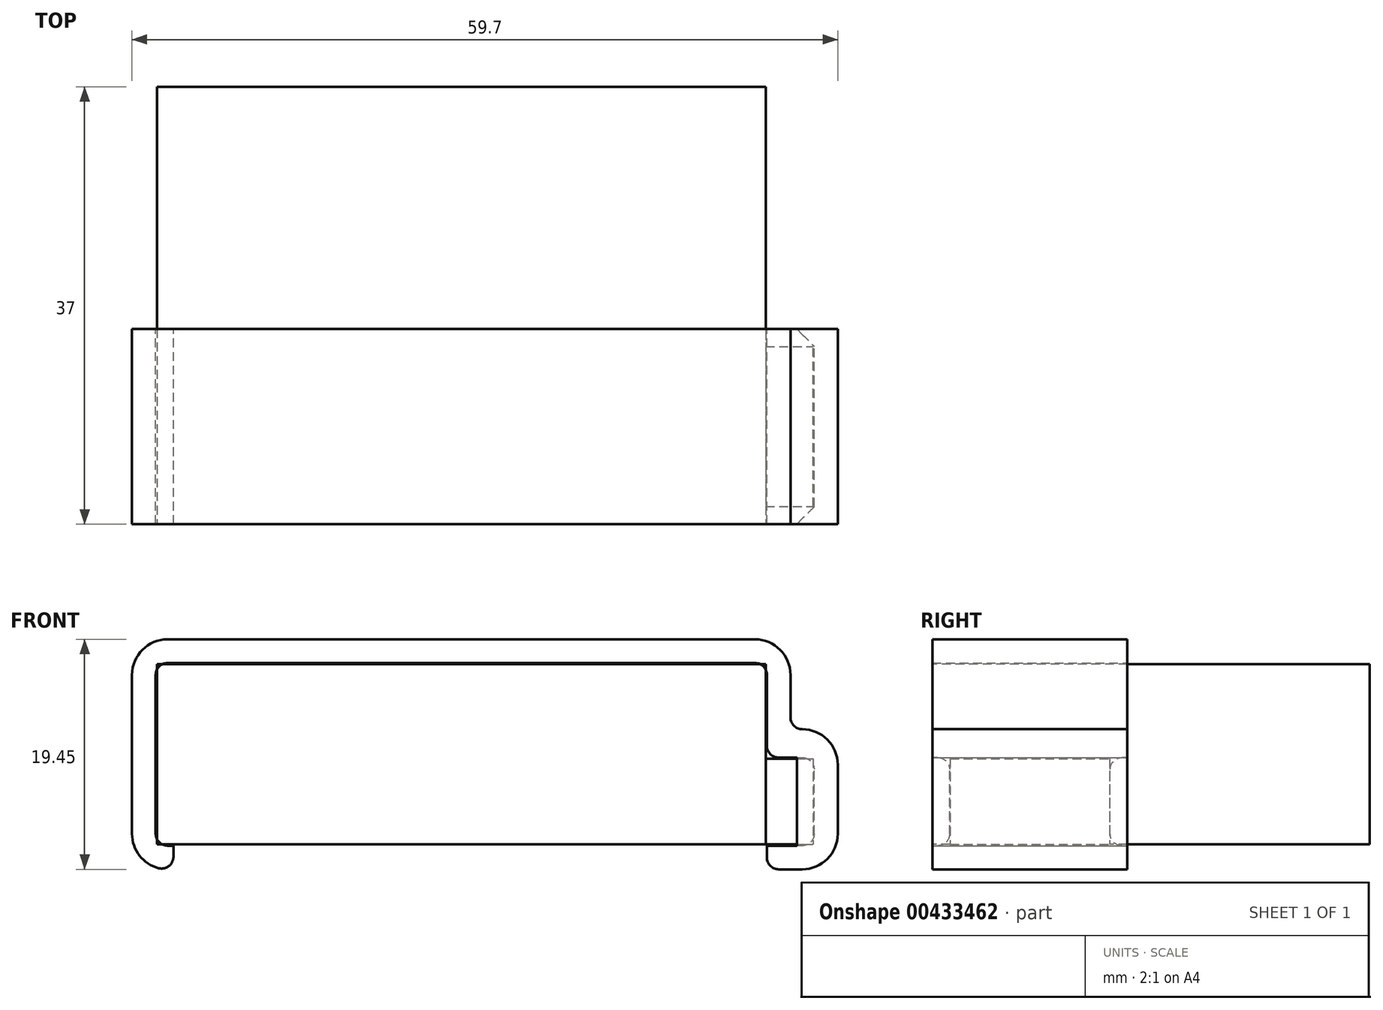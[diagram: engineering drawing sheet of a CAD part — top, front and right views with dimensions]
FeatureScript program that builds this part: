
annotation { "Feature Type Name" : "Feature", "Feature Type Description" : "" }
export const myFeature = defineFeature(function(context is Context, id is Id, definition is map)
    precondition{}
    {
        {
            var Q0;
            Q0=qCreatedBy(makeId("Top.planeOp"),FACE);
            var sketch = newSketch(context, id + "F0", { "sketchPlane" : qUnion([Q0])});
            skLineSegment(sketch, "E0.bottom", {"start": v(-25.75, 18.5) * mm, "end": v(25.75, 18.5) * mm});
            skLineSegment(sketch, "E0.top", {"start": v(-25.75, -18.5) * mm, "end": v(25.75, -18.5) * mm});
            skLineSegment(sketch, "E0.left", {"start": v(-25.75, 18.5) * mm, "end": v(-25.75, -18.5) * mm});
            skLineSegment(sketch, "E0.right", {"start": v(25.75, 18.5) * mm, "end": v(25.75, -18.5) * mm});
            skPoint(sketch, "E0.middle", {"position": v(0, 0) * mm});
            skLineSegment(sketch, "E1.bottom", {"start": v(25.75, -17) * mm, "end": v(29.75, -17) * mm});
            skLineSegment(sketch, "E1.top", {"start": v(25.75, -3.5) * mm, "end": v(29.75, -3.5) * mm});
            skLineSegment(sketch, "E1.left", {"start": v(25.75, -17) * mm, "end": v(25.75, -3.5) * mm});
            skLineSegment(sketch, "E1.right", {"start": v(29.75, -17) * mm, "end": v(29.75, -3.5) * mm});
            skSolve(sketch);
        }
        {
            var Q0;
            Q0=makeQuery(id+"F0.imprint","IMPRINT",FACE,{"disambiguationData":[TD([[makeQuery(id+"F0.imprint","IMPRINT",EDGE,{"derivedFrom":sQuery(id+"F0.wireOp",EDGE,"E1.bottom")}),1.0]])]});
            extrude(context, id + "F1", {"entities" : qUnion([Q0]), "depth" : 7.25 * mm});
        }
        {
            var Q0;
            {var subQ1=sQuery(id+"F0.wireOp",EDGE,"E0.bottom");Q0=makeQuery(id+"F0.imprint","IMPRINT",FACE,{"disambiguationData":[TD([[makeQuery(id+"F0.imprint","IMPRINT",EDGE,{"derivedFrom":subQ1}),-1.0]])]});}
            extrude(context, id + "F2", {"entities" : qUnion([Q0]), "operationType" : NewBodyOperationType.ADD, "depth" : 15.25 * mm});
        }
        {
            var Q0;
            Q0=qCreatedBy(makeId("Front.planeOp"),FACE);
            var sketch = newSketch(context, id + "F3", { "sketchPlane" : qUnion([Q0])});
            skLineSegment(sketch, "E2.0.0", {"start": v(-25.75, 0) * mm, "end": v(25.75, 0) * mm, "construction": true});
            skLineSegment(sketch, "E2.0.1", {"start": v(25.75, 7.25) * mm, "end": v(25.75, 15.25) * mm, "construction": true});
            skLineSegment(sketch, "E2.0.2", {"start": v(25.75, 15.25) * mm, "end": v(-25.75, 15.25) * mm, "construction": true});
            skLineSegment(sketch, "E2.0.3", {"start": v(-25.75, 15.25) * mm, "end": v(-25.75, 0) * mm, "construction": true});
            skLineSegment(sketch, "E3.0.0", {"start": v(25.75, 0) * mm, "end": v(29.75, 0) * mm, "construction": true});
            skLineSegment(sketch, "E3.0.1", {"start": v(29.75, 0) * mm, "end": v(29.75, 7.25) * mm, "construction": true});
            skLineSegment(sketch, "E3.0.2", {"start": v(29.75, 7.25) * mm, "end": v(25.75, 7.25) * mm, "construction": true});
            skLineSegment(sketch, "E4.0", {"start": v(24.85, 15.35) * mm, "end": v(-24.85, 15.35) * mm});
            skLineSegment(sketch, "E4.1", {"start": v(25.85, 7.35) * mm, "end": v(25.85, 14.35) * mm});
            skLineSegment(sketch, "E4.2", {"start": v(-24.85, -0.1) * mm, "end": v(26, -0.1) * mm});
            skLineSegment(sketch, "E4.3", {"start": v(26, -0.1) * mm, "end": v(28.85, -0.1) * mm});
            skLineSegment(sketch, "E4.4", {"start": v(29.85, 0.9) * mm, "end": v(29.85, 6.35) * mm});
            skLineSegment(sketch, "E4.5", {"start": v(-25.85, 14.35) * mm, "end": v(-25.85, 0.9) * mm});
            skLineSegment(sketch, "E4.6", {"start": v(28.85, 7.35) * mm, "end": v(25.85, 7.35) * mm});
            skLineSegment(sketch, "E5.0", {"start": v(24.85, 17.35) * mm, "end": v(-24.85, 17.35) * mm});
            skLineSegment(sketch, "E5.1", {"start": v(27.85, 9.75) * mm, "end": v(27.85, 14.35) * mm});
            skLineSegment(sketch, "E5.2", {"start": v(-24.85, -2.1) * mm, "end": v(26, -2.1) * mm});
            skLineSegment(sketch, "E5.3", {"start": v(26, -2.1) * mm, "end": v(28.85, -2.1) * mm});
            skLineSegment(sketch, "E5.4", {"start": v(31.85, 0.9) * mm, "end": v(31.85, 6.75) * mm});
            skLineSegment(sketch, "E5.5", {"start": v(-27.85, 14.35) * mm, "end": v(-27.85, 0.9) * mm});
            skLineSegment(sketch, "E6", {"start": v(25.85, 7.35) * mm, "end": v(25.85, -0.1) * mm});
            skPoint(sketch, "E7.visualSharp", {"position": v(-25.85, 15.35) * mm});
            skArc(sketch, "E7.filletArc", {"start": v(-24.85, 15.35) * mm, "mid": v(-25.56, 15.06) * mm, "end": v(-25.85, 14.35) * mm});
            skPoint(sketch, "E8.visualSharp", {"position": v(25.85, 15.35) * mm});
            skArc(sketch, "E8.filletArc", {"start": v(25.85, 14.35) * mm, "mid": v(25.56, 15.06) * mm, "end": v(24.85, 15.35) * mm});
            skPoint(sketch, "E9.visualSharp", {"position": v(29.85, 7.35) * mm});
            skArc(sketch, "E9.filletArc", {"start": v(29.85, 6.35) * mm, "mid": v(29.56, 7.06) * mm, "end": v(28.85, 7.35) * mm});
            skPoint(sketch, "E10.visualSharp", {"position": v(29.85, -0.1) * mm});
            skArc(sketch, "E10.filletArc", {"start": v(28.85, -0.1) * mm, "mid": v(29.56, 0.2) * mm, "end": v(29.85, 0.9) * mm});
            skPoint(sketch, "E11.visualSharp", {"position": v(-25.85, -0.1) * mm});
            skArc(sketch, "E11.filletArc", {"start": v(-25.85, 0.9) * mm, "mid": v(-25.56, 0.2) * mm, "end": v(-24.85, -0.1) * mm});
            skPoint(sketch, "E12.visualSharp", {"position": v(-27.85, -2.1) * mm});
            skArc(sketch, "E12.filletArc", {"start": v(-27.85, 0.9) * mm, "mid": v(-26.97, -1.22) * mm, "end": v(-24.85, -2.1) * mm});
            skPoint(sketch, "E13.visualSharp", {"position": v(-27.85, 17.35) * mm});
            skArc(sketch, "E13.filletArc", {"start": v(-24.85, 17.35) * mm, "mid": v(-26.97, 16.47) * mm, "end": v(-27.85, 14.35) * mm});
            skPoint(sketch, "E14.visualSharp", {"position": v(27.85, 17.35) * mm});
            skArc(sketch, "E14.filletArc", {"start": v(27.85, 14.35) * mm, "mid": v(26.97, 16.47) * mm, "end": v(24.85, 17.35) * mm});
            skPoint(sketch, "E15.visualSharp", {"position": v(27.85, 9.75) * mm});
            skPoint(sketch, "E16.visualSharp", {"position": v(31.85, 9.75) * mm});
            skArc(sketch, "E16.filletArc", {"start": v(31.85, 6.75) * mm, "mid": v(30.97, 8.87) * mm, "end": v(28.85, 9.75) * mm});
            skPoint(sketch, "E17.visualSharp", {"position": v(31.85, -2.1) * mm});
            skArc(sketch, "E17.filletArc", {"start": v(28.85, -2.1) * mm, "mid": v(30.97, -1.22) * mm, "end": v(31.85, 0.9) * mm});
            skLineSegment(sketch, "E18", {"start": v(28.85, 9.75) * mm, "end": v(27.85, 9.75) * mm});
            skLineSegment(sketch, "E19", {"start": v(25.85, -0.1) * mm, "end": v(25.85, -2.1) * mm});
            skLineSegment(sketch, "E20", {"start": v(-24.35, -0.1) * mm, "end": v(-24.35, -2.1) * mm});
            skSolve(sketch);
        }
        {
            var Q0;
            Q0=makeQuery(id+"F3.imprint","IMPRINT",FACE,{"disambiguationData":[TD([[makeQuery(id+"F3.imprint","IMPRINT",EDGE,{"derivedFrom":sQuery(id+"F3.wireOp",EDGE,"E4.0")}),-1.0]])]});
            var Q1;
            Q1=makeQuery(id+"F2.opExtrude","SWEPT_FACE",FACE,{"disambiguationData":[OSD([sQuery(id+"F0.wireOp",EDGE,"E0.top")])]});
            extrude(context, id + "F4", {"entities" : qUnion([Q0]), "endBound" : BoundingType.UP_TO_SURFACE, "endBoundEntityFace" : qUnion([Q1]), "depth" : 25 * mm, "hasSecondDirection" : true, "secondDirectionOppositeDirection" : false, "secondDirectionDepth" : 2 * mm});
        }
        {
            var Q0;
            Q0=qCreatedBy(makeId("Top.planeOp"),FACE);
            var sketch = newSketch(context, id + "F5", { "sketchPlane" : qUnion([Q0])});
            skLineSegment(sketch, "E21.0.1", {"start": v(29.85, -18.5) * mm, "end": v(29.85, -2) * mm, "construction": true});
            skLineSegment(sketch, "E21.0.3", {"start": v(29.85, -2) * mm, "end": v(29.85, -18.5) * mm, "construction": true});
            skLineSegment(sketch, "E22.0.0", {"start": v(25.75, -17) * mm, "end": v(29.75, -17) * mm, "construction": true});
            skLineSegment(sketch, "E22.0.2", {"start": v(29.75, -17) * mm, "end": v(25.75, -17) * mm, "construction": true});
            skLineSegment(sketch, "E23.0.0", {"start": v(29.75, -3.5) * mm, "end": v(25.75, -3.5) * mm, "construction": true});
            skLineSegment(sketch, "E23.0.2", {"start": v(25.75, -3.5) * mm, "end": v(29.75, -3.5) * mm, "construction": true});
            skLineSegment(sketch, "E24", {"start": v(29.85, -18.5) * mm, "end": v(29.85, -17.04) * mm});
            skLineSegment(sketch, "E25", {"start": v(29.85, -17.04) * mm, "end": v(28.4, -18.5) * mm});
            skLineSegment(sketch, "E26", {"start": v(28.4, -18.5) * mm, "end": v(29.85, -18.5) * mm});
            skLineSegment(sketch, "E27", {"start": v(29.85, -2) * mm, "end": v(28.4, -2) * mm});
            skLineSegment(sketch, "E28", {"start": v(28.4, -2) * mm, "end": v(29.85, -3.46) * mm});
            skLineSegment(sketch, "E29", {"start": v(29.85, -3.46) * mm, "end": v(29.85, -2) * mm});
            skLineSegment(sketch, "E30.0.0", {"start": v(26.5, -2) * mm, "end": v(26.5, -18.5) * mm, "construction": true});
            skLineSegment(sketch, "E30.0.2", {"start": v(26.5, -18.5) * mm, "end": v(26.5, -2) * mm, "construction": true});
            skSolve(sketch);
        }
        {
            var Q0;
            Q0=makeQuery(id+"F5.imprint","IMPRINT",FACE,{"disambiguationData":[TD([[makeQuery(id+"F5.imprint","IMPRINT",EDGE,{"derivedFrom":sQuery(id+"F5.wireOp",EDGE,"E27")}),1.0]])]});
            var Q1;
            Q1=makeQuery(id+"F5.imprint","IMPRINT",FACE,{"disambiguationData":[TD([[makeQuery(id+"F5.imprint","IMPRINT",EDGE,{"derivedFrom":sQuery(id+"F5.wireOp",EDGE,"E24")}),1.0]])]});
            var Q2;
            Q2=makeQuery(id+"F4.opExtrude","SWEPT_FACE",FACE,{"disambiguationData":[OSD([sQuery(id+"F3.wireOp",EDGE,"E4.3")])]});
            var Q3;
            Q3=makeQuery(id+"F4.opExtrude","SWEPT_FACE",FACE,{"disambiguationData":[OSD([sQuery(id+"F3.wireOp",EDGE,"E4.6")])]});
            extrude(context, id + "F6", {"entities" : qUnion([Q0, Q1]), "operationType" : NewBodyOperationType.ADD, "endBound" : BoundingType.UP_TO_SURFACE, "oppositeDirection" : true, "endBoundEntityFace" : qUnion([Q2]), "depth" : 25 * mm, "hasSecondDirection" : true, "secondDirectionBound" : SecondDirectionBoundingType.UP_TO_SURFACE, "secondDirectionOppositeDirection" : false, "secondDirectionBoundEntityFace" : qUnion([Q3]), "secondDirectionDepth" : 25 * mm});
        }
        {
            var Q0;
            Q0=makeQuery(id+"F4.opExtrude","SWEPT_EDGE",EDGE,{"disambiguationData":[OSD([sQuery(id+"F3.wireOp",EDGE,"E4.1"),sQuery(id+"F3.wireOp",EDGE,"E4.6"),sQuery(id+"F3.wireOp",EDGE,"E6")])]});
            var Q1;
            Q1=makeQuery(id+"F4.opExtrude","SWEPT_EDGE",EDGE,{"disambiguationData":[OSD([sQuery(id+"F3.wireOp",EDGE,"E5.1"),sQuery(id+"F3.wireOp",EDGE,"E18")])]});
            var Q2;
            Q2=makeQuery(id+"F4.opExtrude","SWEPT_EDGE",EDGE,{"disambiguationData":[OSD([sQuery(id+"F3.wireOp",EDGE,"E5.3"),sQuery(id+"F3.wireOp",EDGE,"E19")])]});
            var Q3;
            Q3=makeQuery(id+"F4.opExtrude","SWEPT_EDGE",EDGE,{"disambiguationData":[OSD([sQuery(id+"F3.wireOp",EDGE,"E5.2"),sQuery(id+"F3.wireOp",EDGE,"E20")])]});
            fillet(context, id + "F7", {"entities" : qUnion([Q0, Q1, Q2, Q3]), "radius" : 1 * mm, "tangentPropagation" : true, "allowEdgeOverflow" : false});
        }
    });
